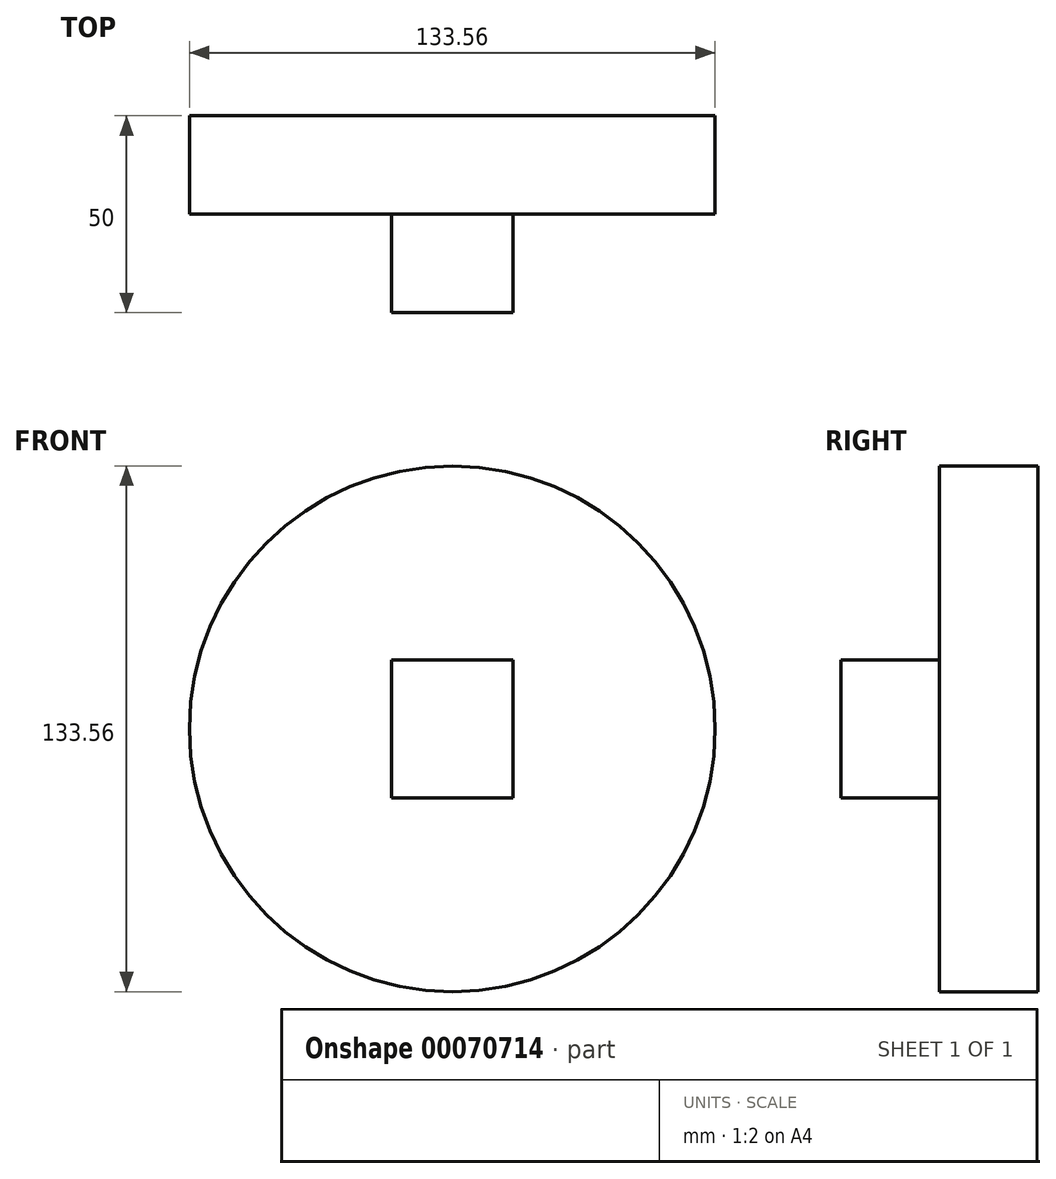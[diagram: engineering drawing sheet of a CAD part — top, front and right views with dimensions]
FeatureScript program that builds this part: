
annotation { "Feature Type Name" : "Feature", "Feature Type Description" : "" }
export const myFeature = defineFeature(function(context is Context, id is Id, definition is map)
    precondition{}
    {
        {
            var Q0;
            Q0=qCreatedBy(makeId("Front.planeOp"),FACE);
            var sketch = newSketch(context, id + "F0", { "sketchPlane" : qUnion([Q0])});
            skCircle(sketch, "E0", {"center": v(66.78, 0) * mm, "radius": 66.78 * mm});
            skSolve(sketch);
        }
        {
            var Q0;
            Q0=makeQuery(id+"F0.imprint","IMPRINT",FACE,{"disambiguationData":[TD([[makeQuery(id+"F0.imprint","IMPRINT",EDGE,{"derivedFrom":sQuery(id+"F0.wireOp",EDGE,"E0")}),1.0]])]});
            extrude(context, id + "F1", {"entities" : qUnion([Q0]), "depth" : 25 * mm});
        }
        {
            var Q0;
            Q0=makeQuery(id+"F1.opExtrude","CAP_FACE",FACE,{"disambiguationData":[OSD([sQuery(id+"F0.wireOp",EDGE,"E0")])],"isStart":false});
            var sketch = newSketch(context, id + "F2", { "sketchPlane" : qUnion([Q0])});
            skLineSegment(sketch, "E1.rect.bottom", {"start": v(82.17, 17.5) * mm, "end": v(51.39, 17.5) * mm});
            skLineSegment(sketch, "E1.rect.top", {"start": v(82.17, -17.5) * mm, "end": v(51.39, -17.5) * mm});
            skLineSegment(sketch, "E1.rect.left", {"start": v(82.17, 17.5) * mm, "end": v(82.17, -17.5) * mm});
            skLineSegment(sketch, "E1.rect.right", {"start": v(51.39, 17.5) * mm, "end": v(51.39, -17.5) * mm});
            skPoint(sketch, "E1.rect.middle", {"position": v(66.78, 0) * mm});
            skSolve(sketch);
        }
        {
            var Q0;
            Q0 = qSketchRegion(id + "F2", true);
            extrude(context, id + "F3", {"entities" : qUnion([Q0]), "operationType" : NewBodyOperationType.ADD, "depth" : 25 * mm});
        }
    });
